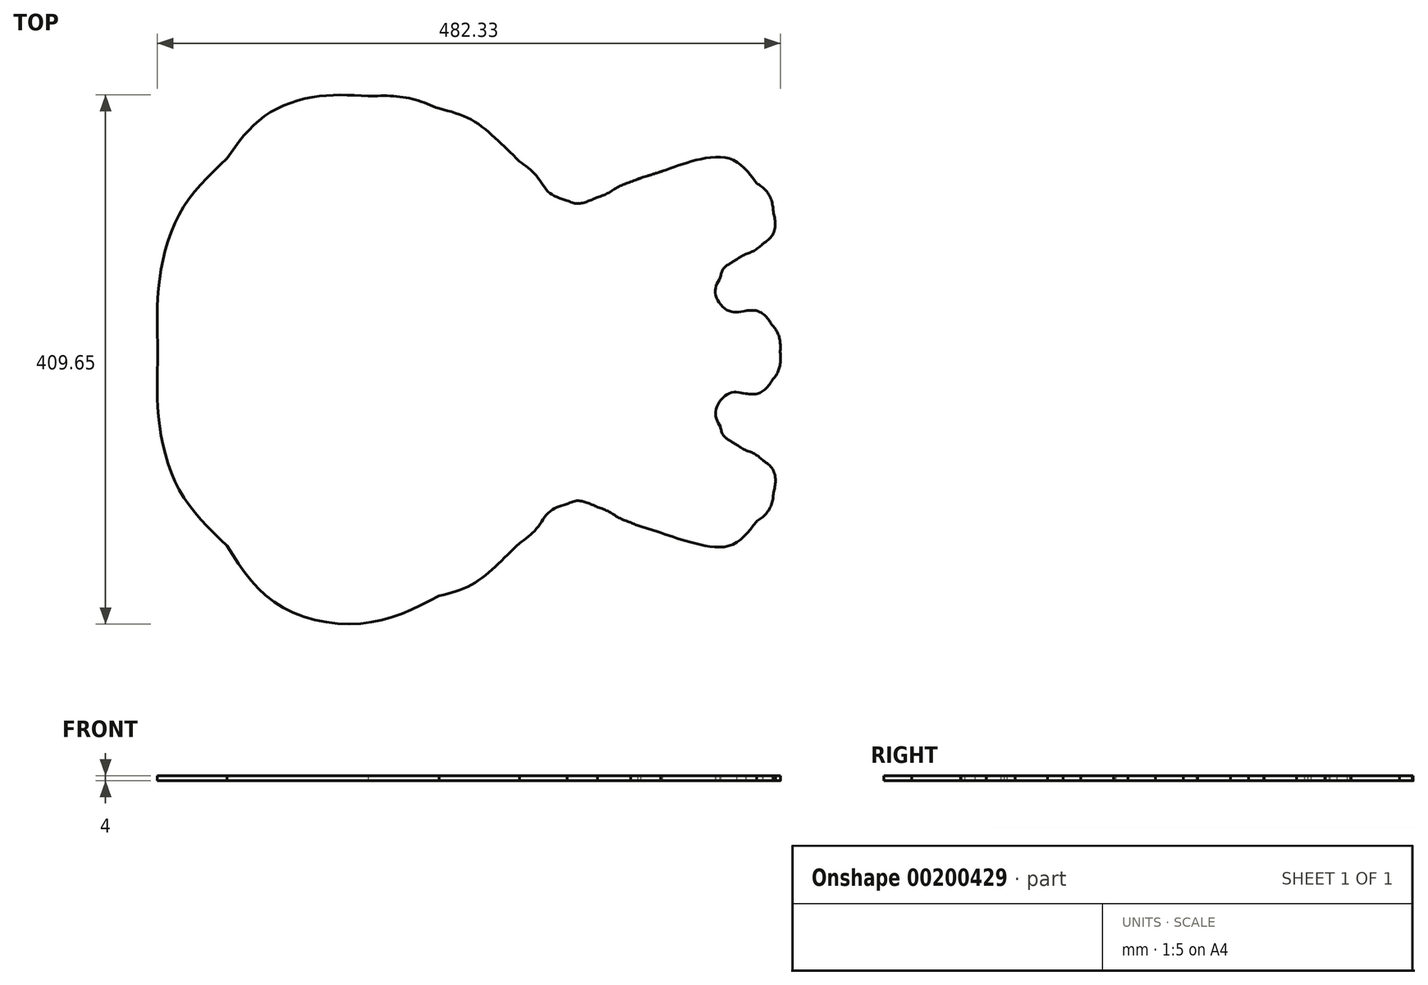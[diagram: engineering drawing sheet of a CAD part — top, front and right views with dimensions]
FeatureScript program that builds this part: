
annotation { "Feature Type Name" : "Feature", "Feature Type Description" : "" }
export const myFeature = defineFeature(function(context is Context, id is Id, definition is map)
    precondition{}
    {
        {
            var Q0;
            Q0=qCreatedBy(makeId("Top.planeOp"),FACE);
            var sketch = newSketch(context, id + "F0", { "sketchPlane" : qUnion([Q0])});
            skFitSpline(sketch, "E0", {"points": [v(-78.04, 198.25) * mm, v(-119.04, 197.89) * mm, v(-160, 181.57) * mm, v(-187.36, 150.03) * mm]});
            skFitSpline(sketch, "E1", {"points": [v(-187.36, 150.03) * mm, v(-187.36, 150.03) * mm, v(-187.36, 150.03) * mm, v(-187.37, 150.03) * mm]});
            skFitSpline(sketch, "E2", {"points": [v(-187.37, 150.03) * mm, v(-223.16, 108.91) * mm, v(-239.83, 53.35) * mm, v(-240.8, -0.14) * mm]});
            skFitSpline(sketch, "E3", {"points": [v(-240.8, -0.14) * mm, v(-240.8, -0.2) * mm, v(-240.8, -0.26) * mm, v(-240.8, -0.32) * mm]});
            skFitSpline(sketch, "E4", {"points": [v(-240.8, -0.32) * mm, v(-239.84, -53.82) * mm, v(-222.97, -108.9) * mm, v(-187.2, -150) * mm]});
            skFitSpline(sketch, "E5", {"points": [v(-187.2, -150) * mm, v(-147.44, -195.82) * mm, v(-79.11, -209.65) * mm, v(-23.3, -188.74) * mm]});
            skFitSpline(sketch, "E6", {"points": [v(-23.13, -188.68) * mm, v(1.06, -180.57) * mm, v(21.28, -165.04) * mm, v(38.94, -147.97) * mm]});
            skFitSpline(sketch, "E7", {"points": [v(38.94, -147.97) * mm, v(52.03, -136.9) * mm, v(62.2, -123.64) * mm, v(75.9, -117.52) * mm]});
            skFitSpline(sketch, "E8", {"points": [v(75.9, -117.52) * mm, v(83.86, -115.06) * mm, v(91.4, -116.61) * mm, v(99.54, -119.9) * mm]});
            skFitSpline(sketch, "E9", {"points": [v(99.54, -119.9) * mm, v(107.76, -123.22) * mm, v(116.2, -128.33) * mm, v(125.15, -131.87) * mm]});
            skFitSpline(sketch, "E10", {"points": [v(125.15, -131.87) * mm, v(132.73, -135) * mm, v(140.63, -137.38) * mm, v(148.4, -139.83) * mm]});
            skFitSpline(sketch, "E11", {"points": [v(148.4, -139.83) * mm, v(148.4, -139.83) * mm, v(148.4, -139.83) * mm, v(148.4, -139.83) * mm]});
            skFitSpline(sketch, "E12", {"points": [v(148.4, -139.83) * mm, v(148.4, -139.83) * mm, v(148.4, -139.83) * mm, v(148.4, -139.83) * mm]});
            skFitSpline(sketch, "E13", {"points": [v(148.4, -139.83) * mm, v(172.53, -147.47) * mm, v(202.04, -149.7) * mm, v(222.44, -131.04) * mm]});
            skLineSegment(sketch, "E14", {"start": v(-23.3, -188.74) * mm, "end": v(-23.13, -188.68) * mm});
            skLineSegment(sketch, "E15", {"start": v(-23.13, -188.68) * mm, "end": v(-23.3, -188.74) * mm});
            skFitSpline(sketch, "E16", {"points": [v(222.51, -130.98) * mm, v(229.46, -125.63) * mm, v(234.2, -117.51) * mm, v(235.64, -108.84) * mm]});
            skFitSpline(sketch, "E17", {"points": [v(235.64, -108.84) * mm, v(237.08, -100.14) * mm, v(234.9, -90.51) * mm, v(227.5, -83.85) * mm]});
            skFitSpline(sketch, "E18", {"points": [v(227.5, -83.85) * mm, v(227.4, -83.76) * mm, v(227.3, -83.68) * mm, v(227.2, -83.6) * mm]});
            skFitSpline(sketch, "E19", {"points": [v(227.2, -83.6) * mm, v(220.69, -78.57) * mm, v(213.18, -75.42) * mm, v(207.1, -71.7) * mm]});
            skFitSpline(sketch, "E20", {"points": [v(207.1, -71.7) * mm, v(201, -68) * mm, v(196.59, -64.15) * mm, v(194.63, -57.86) * mm]});
            skFitSpline(sketch, "E21", {"points": [v(194.63, -57.86) * mm, v(194.63, -57.86) * mm, v(194.63, -57.86) * mm, v(194.63, -57.86) * mm]});
            skFitSpline(sketch, "E22", {"points": [v(194.63, -57.86) * mm, v(190.81, -45.54) * mm, v(200.8, -32.1) * mm, v(214.1, -32.1) * mm]});
            skFitSpline(sketch, "E23", {"points": [v(214.1, -32.1) * mm, v(214.1, -32.1) * mm, v(214.1, -32.1) * mm, v(214.1, -32.1) * mm]});
            skFitSpline(sketch, "E24", {"points": [v(214.1, -32.1) * mm, v(223, -32.11) * mm, v(230.23, -27.74) * mm, v(234.6, -21.6) * mm]});
            skFitSpline(sketch, "E25", {"points": [v(234.6, -21.6) * mm, v(238.99, -15.45) * mm, v(240.88, -7.74) * mm, v(240.8, -0.1) * mm]});
            skFitSpline(sketch, "E26", {"points": [v(240.8, -0.1) * mm, v(240.71, 7.56) * mm, v(238.65, 15.24) * mm, v(234.27, 21.38) * mm]});
            skFitSpline(sketch, "E27", {"points": [v(234.27, 21.38) * mm, v(229.9, 27.51) * mm, v(222.8, 31.98) * mm, v(214.13, 32.07) * mm]});
            skLineSegment(sketch, "E28", {"start": v(222.44, -131.04) * mm, "end": v(222.51, -130.98) * mm});
            skLineSegment(sketch, "E29", {"start": v(222.51, -130.98) * mm, "end": v(222.44, -131.04) * mm});
            skFitSpline(sketch, "E30", {"points": [v(214.18, 32.07) * mm, v(200.38, 32.38) * mm, v(190.63, 45.52) * mm, v(194.46, 57.9) * mm]});
            skFitSpline(sketch, "E31", {"points": [v(194.46, 57.9) * mm, v(194.46, 57.9) * mm, v(194.46, 57.9) * mm, v(194.46, 57.9) * mm]});
            skFitSpline(sketch, "E32", {"points": [v(194.46, 57.9) * mm, v(196.42, 64.19) * mm, v(200.84, 68.03) * mm, v(206.92, 71.74) * mm]});
            skFitSpline(sketch, "E33", {"points": [v(206.92, 71.74) * mm, v(213.01, 75.45) * mm, v(220.52, 78.6) * mm, v(227.04, 83.64) * mm]});
            skFitSpline(sketch, "E34", {"points": [v(227.04, 83.64) * mm, v(227.14, 83.72) * mm, v(227.23, 83.8) * mm, v(227.33, 83.88) * mm]});
            skFitSpline(sketch, "E35", {"points": [v(227.33, 83.88) * mm, v(234.73, 90.55) * mm, v(236.91, 100.17) * mm, v(235.47, 108.87) * mm]});
            skFitSpline(sketch, "E36", {"points": [v(235.47, 108.87) * mm, v(234.03, 117.58) * mm, v(229.27, 125.73) * mm, v(222.28, 131.07) * mm]});
            skLineSegment(sketch, "E37", {"start": v(214.13, 32.07) * mm, "end": v(214.18, 32.07) * mm});
            skLineSegment(sketch, "E38", {"start": v(214.18, 32.07) * mm, "end": v(214.13, 32.07) * mm});
            skFitSpline(sketch, "E39", {"points": [v(222.65, 130.76) * mm, v(202.38, 149.65) * mm, v(173.51, 148.17) * mm, v(149.67, 140.17) * mm]});
            skFitSpline(sketch, "E40", {"points": [v(149.67, 140.17) * mm, v(147.85, 139.64) * mm, v(141.74, 137.66) * mm, v(138.38, 136.67) * mm]});
            skFitSpline(sketch, "E41", {"points": [v(138.38, 136.67) * mm, v(138.34, 136.66) * mm, v(138.3, 136.65) * mm, v(138.26, 136.63) * mm]});
            skFitSpline(sketch, "E42", {"points": [v(138.26, 136.63) * mm, v(130.58, 134.17) * mm, v(132.83, 134.84) * mm, v(125.1, 131.95) * mm]});
            skFitSpline(sketch, "E43", {"points": [v(125.1, 131.95) * mm, v(125.07, 131.94) * mm, v(125.04, 131.93) * mm, v(125, 131.92) * mm]});
            skFitSpline(sketch, "E44", {"points": [v(125, 131.92) * mm, v(116.05, 128.38) * mm, v(107.6, 123.26) * mm, v(99.38, 119.94) * mm]});
            skFitSpline(sketch, "E45", {"points": [v(99.38, 119.94) * mm, v(91.23, 116.65) * mm, v(83.7, 115.1) * mm, v(75.73, 117.55) * mm]});
            skFitSpline(sketch, "E46", {"points": [v(75.73, 117.55) * mm, v(62.04, 123.68) * mm, v(51.86, 136.93) * mm, v(38.77, 148) * mm]});
            skFitSpline(sketch, "E47", {"points": [v(38.77, 148) * mm, v(21.11, 165.07) * mm, v(0.9, 180.6) * mm, v(-23.3, 188.71) * mm]});
            skLineSegment(sketch, "E48", {"start": v(222.28, 131.07) * mm, "end": v(222.65, 130.76) * mm});
            skLineSegment(sketch, "E49", {"start": v(222.65, 130.76) * mm, "end": v(222.28, 131.07) * mm});
            skFitSpline(sketch, "E50", {"points": [v(-23.3, 188.71) * mm, v(-40.74, 195.28) * mm, v(-59.41, 198.41) * mm, v(-78.04, 198.25) * mm]});
            skLineSegment(sketch, "E51", {"start": v(-23.3, 188.71) * mm, "end": v(-23.3, 188.71) * mm});
            skSolve(sketch);
        }
        {
            var Q0;
            Q0 = qSketchRegion(id + "F0", true);
            extrude(context, id + "F1", {"entities" : qUnion([Q0]), "depth" : 4 * mm});
        }
    });
